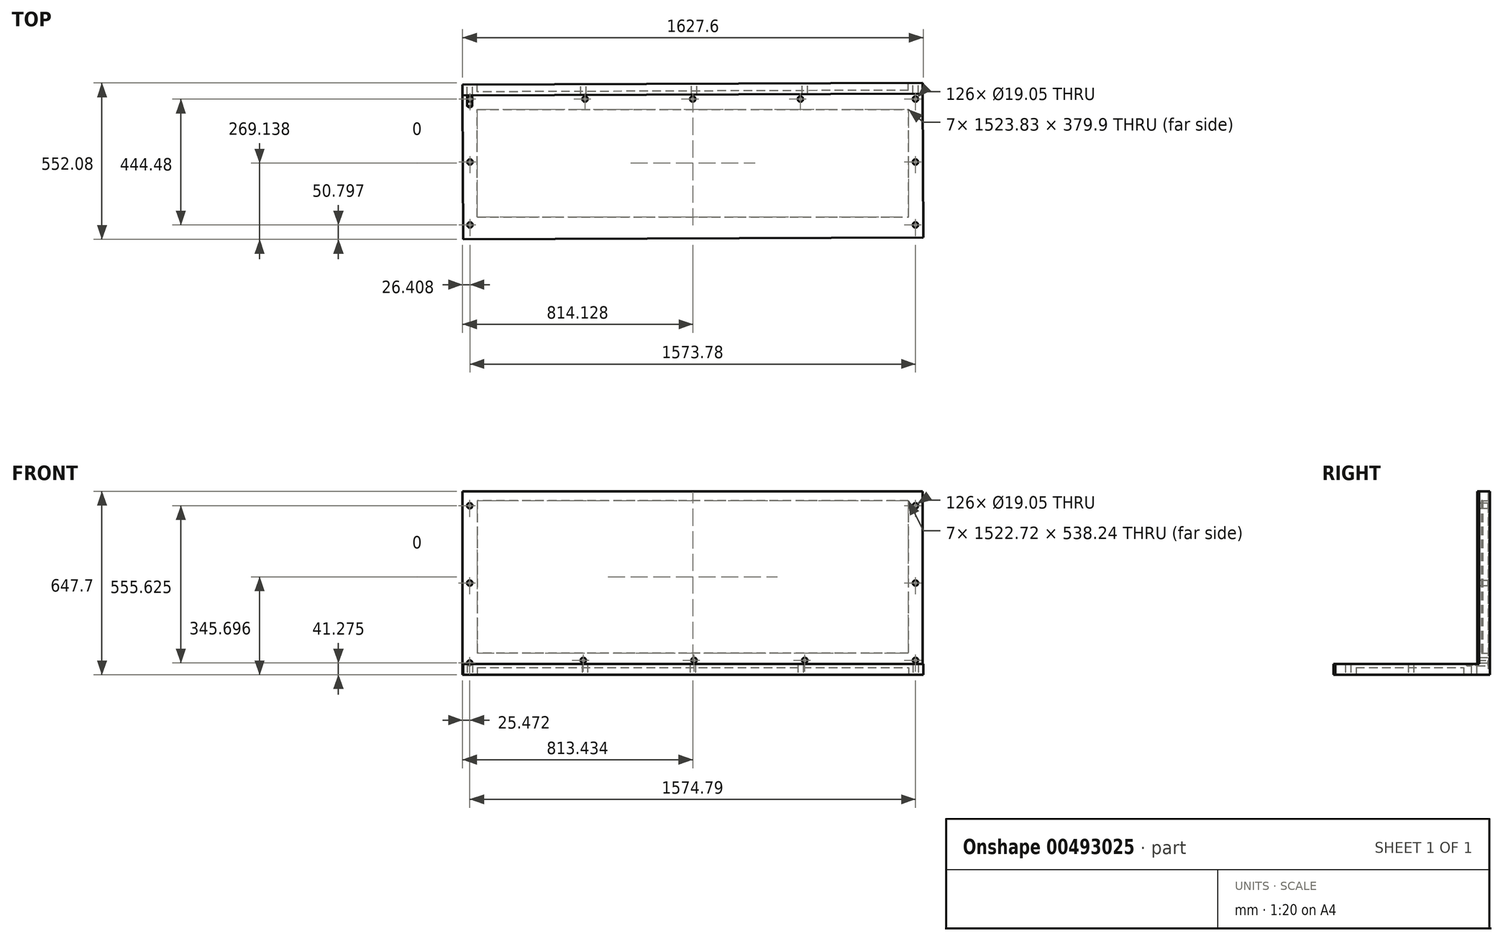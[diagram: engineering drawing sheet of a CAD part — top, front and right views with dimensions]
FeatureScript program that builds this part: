
annotation { "Feature Type Name" : "Feature", "Feature Type Description" : "" }
export const myFeature = defineFeature(function(context is Context, id is Id, definition is map)
    precondition{}
    {
        {
            var Q0;
            Q0=qCreatedBy(makeId("Top.planeOp"),FACE);
            var sketch = newSketch(context, id + "F0", { "sketchPlane" : qUnion([Q0])});
            skLineSegment(sketch, "E0", {"start": v(-1490.15, -82.87) * mm, "end": v(-1490.15, -540.07) * mm});
            skLineSegment(sketch, "E1", {"start": v(-1490.15, -540.07) * mm, "end": v(-1452.05, -540.07) * mm});
            skLineSegment(sketch, "E2", {"start": v(-1490.15, -82.87) * mm, "end": v(33.85, -82.87) * mm});
            skLineSegment(sketch, "E3", {"start": v(33.85, -82.87) * mm, "end": v(33.85, -540.07) * mm});
            skLineSegment(sketch, "E4", {"start": v(33.85, -540.07) * mm, "end": v(-4.25, -540.07) * mm});
            skLineSegment(sketch, "E5", {"start": v(-1445.7, -127.32) * mm, "end": v(-1452.05, -540.07) * mm});
            skLineSegment(sketch, "E6", {"start": v(-10.6, -127.32) * mm, "end": v(-4.25, -540.07) * mm});
            skLineSegment(sketch, "E7", {"start": v(-1445.7, -127.32) * mm, "end": v(-750.38, -127.32) * mm});
            skLineSegment(sketch, "E8", {"start": v(-10.6, -127.32) * mm, "end": v(-705.93, -127.32) * mm});
            skLineSegment(sketch, "E9", {"start": v(-705.93, -127.32) * mm, "end": v(-709.1, -540.07) * mm});
            skLineSegment(sketch, "E10", {"start": v(-750.38, -127.32) * mm, "end": v(-747.2, -540.07) * mm});
            skLineSegment(sketch, "E11", {"start": v(-709.1, -540.07) * mm, "end": v(-747.2, -540.07) * mm});
            skLineSegment(sketch, "E12", {"start": v(33.85, -540.07) * mm, "end": v(33.85, -590.87) * mm});
            skLineSegment(sketch, "E13", {"start": v(82.6, -32.07) * mm, "end": v(84.65, -590.87) * mm});
            skLineSegment(sketch, "E14", {"start": v(-1540.94, -35.7) * mm, "end": v(-1540.94, -594.5) * mm});
            skLineSegment(sketch, "E15", {"start": v(-1540.94, -35.7) * mm, "end": v(82.6, -32.07) * mm});
            skLineSegment(sketch, "E16", {"start": v(-1540.94, -594.5) * mm, "end": v(84.65, -590.87) * mm});
            skSolve(sketch);
        }
        {
            var Q0;
            Q0=makeQuery(id+"F0.imprint","IMPRINT",FACE,{"disambiguationData":[TD([[makeQuery(id+"F0.imprint","IMPRINT",EDGE,{"derivedFrom":sQuery(id+"F0.wireOp",EDGE,"E0")}),-1.0]])]});
            extrude(context, id + "F1", {"entities" : qUnion([Q0]), "depth" : -609.6 * mm});
        }
        {
            var Q0;
            Q0=makeQuery(id+"F1.opExtrude","CAP_FACE",FACE,{"disambiguationData":[OSD([sQuery(id+"F0.wireOp",EDGE,"E0"),sQuery(id+"F0.wireOp",EDGE,"E1"),sQuery(id+"F0.wireOp",EDGE,"E2"),sQuery(id+"F0.wireOp",EDGE,"E3"),sQuery(id+"F0.wireOp",EDGE,"E4"),sQuery(id+"F0.wireOp",EDGE,"E5"),sQuery(id+"F0.wireOp",EDGE,"E6"),sQuery(id+"F0.wireOp",EDGE,"E7"),sQuery(id+"F0.wireOp",EDGE,"E8"),sQuery(id+"F0.wireOp",EDGE,"E9"),sQuery(id+"F0.wireOp",EDGE,"E10"),sQuery(id+"F0.wireOp",EDGE,"E11"),sQuery(id+"F0.wireOp",EDGE,"E13"),sQuery(id+"F0.wireOp",EDGE,"E14"),sQuery(id+"F0.wireOp",EDGE,"E15"),sQuery(id+"F0.wireOp",EDGE,"E16")])],"isStart":true});
            var sketch = newSketch(context, id + "F2", { "sketchPlane" : qUnion([Q0])});
            skLineSegment(sketch, "E17.bottom", {"start": v(-653.62, -154.54) * mm, "end": v(-44.02, -154.54) * mm});
            skLineSegment(sketch, "E17.top", {"start": v(-653.62, -539.96) * mm, "end": v(-44.02, -539.96) * mm});
            skLineSegment(sketch, "E17.left", {"start": v(-653.62, -154.54) * mm, "end": v(-653.62, -539.96) * mm});
            skLineSegment(sketch, "E17.right", {"start": v(-44.02, -154.54) * mm, "end": v(-44.02, -539.96) * mm});
            skLineSegment(sketch, "E18.bottom", {"start": v(-791.66, -154.54) * mm, "end": v(-1401.26, -154.54) * mm});
            skLineSegment(sketch, "E18.top", {"start": v(-791.66, -534.45) * mm, "end": v(-1401.26, -534.45) * mm});
            skLineSegment(sketch, "E18.left", {"start": v(-791.66, -154.54) * mm, "end": v(-791.66, -534.45) * mm});
            skLineSegment(sketch, "E18.right", {"start": v(-1401.26, -154.54) * mm, "end": v(-1401.26, -534.45) * mm});
            skSolve(sketch);
        }
        {
            var Q0;
            Q0=makeQuery(id+"F2.imprint","IMPRINT",FACE,{"disambiguationData":[TD([[makeQuery(id+"F2.imprint","IMPRINT",EDGE,{"derivedFrom":sQuery(id+"F2.wireOp",EDGE,"E18.bottom")}),1.0]])]});
            extrude(context, id + "F3", {"entities" : qUnion([Q0]), "operationType" : NewBodyOperationType.REMOVE, "oppositeDirection" : true, "depth" : 609.6 * mm});
        }
        {
            var Q0;
            Q0=makeQuery(id+"F1.opExtrude","CAP_FACE",FACE,{"disambiguationData":[OSD([sQuery(id+"F0.wireOp",EDGE,"E0"),sQuery(id+"F0.wireOp",EDGE,"E1"),sQuery(id+"F0.wireOp",EDGE,"E2"),sQuery(id+"F0.wireOp",EDGE,"E3"),sQuery(id+"F0.wireOp",EDGE,"E4"),sQuery(id+"F0.wireOp",EDGE,"E5"),sQuery(id+"F0.wireOp",EDGE,"E6"),sQuery(id+"F0.wireOp",EDGE,"E7"),sQuery(id+"F0.wireOp",EDGE,"E8"),sQuery(id+"F0.wireOp",EDGE,"E9"),sQuery(id+"F0.wireOp",EDGE,"E10"),sQuery(id+"F0.wireOp",EDGE,"E11"),sQuery(id+"F0.wireOp",EDGE,"E13"),sQuery(id+"F0.wireOp",EDGE,"E14"),sQuery(id+"F0.wireOp",EDGE,"E15"),sQuery(id+"F0.wireOp",EDGE,"E16")])],"isStart":true});
            var sketch = newSketch(context, id + "F4", { "sketchPlane" : qUnion([Q0])});
            skLineSegment(sketch, "E19.bottom", {"start": v(-667.58, -154.54) * mm, "end": v(-57.98, -154.54) * mm});
            skLineSegment(sketch, "E19.top", {"start": v(-667.58, -534.45) * mm, "end": v(-57.98, -534.45) * mm});
            skLineSegment(sketch, "E19.left", {"start": v(-667.58, -154.54) * mm, "end": v(-667.58, -534.45) * mm});
            skLineSegment(sketch, "E19.right", {"start": v(-57.98, -154.54) * mm, "end": v(-57.98, -534.45) * mm});
            skSolve(sketch);
        }
        {
            var Q0;
            Q0=makeQuery(id+"F4.imprint","IMPRINT",FACE,{"disambiguationData":[TD([[makeQuery(id+"F4.imprint","IMPRINT",EDGE,{"derivedFrom":sQuery(id+"F4.wireOp",EDGE,"E19.bottom")}),-1.0]])]});
            extrude(context, id + "F5", {"entities" : qUnion([Q0]), "operationType" : NewBodyOperationType.REMOVE, "oppositeDirection" : true, "depth" : 609.6 * mm});
        }
        {
            var Q0;
            Q0=makeQuery(id+"F1.opExtrude","CAP_FACE",FACE,{"disambiguationData":[OSD([sQuery(id+"F0.wireOp",EDGE,"E0"),sQuery(id+"F0.wireOp",EDGE,"E1"),sQuery(id+"F0.wireOp",EDGE,"E2"),sQuery(id+"F0.wireOp",EDGE,"E3"),sQuery(id+"F0.wireOp",EDGE,"E4"),sQuery(id+"F0.wireOp",EDGE,"E5"),sQuery(id+"F0.wireOp",EDGE,"E6"),sQuery(id+"F0.wireOp",EDGE,"E7"),sQuery(id+"F0.wireOp",EDGE,"E8"),sQuery(id+"F0.wireOp",EDGE,"E9"),sQuery(id+"F0.wireOp",EDGE,"E10"),sQuery(id+"F0.wireOp",EDGE,"E11"),sQuery(id+"F0.wireOp",EDGE,"E13"),sQuery(id+"F0.wireOp",EDGE,"E14"),sQuery(id+"F0.wireOp",EDGE,"E15"),sQuery(id+"F0.wireOp",EDGE,"E16")])],"isStart":true});
            var sketch = newSketch(context, id + "F6", { "sketchPlane" : qUnion([Q0])});
            skLineSegment(sketch, "E20", {"start": v(-1540.94, -82.87) * mm, "end": v(82.78, -82.87) * mm});
            skLineSegment(sketch, "E21", {"start": v(82.78, -82.87) * mm, "end": v(82.6, -32.07) * mm});
            skLineSegment(sketch, "E22", {"start": v(-1540.94, -35.7) * mm, "end": v(82.6, -32.07) * mm});
            skLineSegment(sketch, "E23", {"start": v(-1540.94, -35.7) * mm, "end": v(-1540.94, -82.87) * mm});
            skSolve(sketch);
        }
        {
            var Q0;
            Q0=qSketchRegion(id+"F6",true);
            extrude(context, id + "F7", {"entities" : qUnion([Q0]), "operationType" : NewBodyOperationType.REMOVE, "oppositeDirection" : true, "depth" : 609.6 * mm});
        }
        {
            var Q0;
            Q0=makeQuery(id+"F1.opExtrude","SWEPT_FACE",FACE,{"disambiguationData":[OSD([sQuery(id+"F0.wireOp",EDGE,"E13")])]});
            var sketch = newSketch(context, id + "F8", { "sketchPlane" : qUnion([Q0])});
            skLineSegment(sketch, "E24.bottom", {"start": v(-38.1, 0) * mm, "end": v(0, 0) * mm});
            skLineSegment(sketch, "E24.top", {"start": v(-38.1, -609.6) * mm, "end": v(0, -609.6) * mm});
            skLineSegment(sketch, "E24.left", {"start": v(-38.1, 0) * mm, "end": v(-38.1, -609.6) * mm});
            skLineSegment(sketch, "E24.right", {"start": v(0, 0) * mm, "end": v(0, -609.6) * mm});
            skLineSegment(sketch, "E25.bottom", {"start": v(0, -609.6) * mm, "end": v(-546.1, -609.6) * mm});
            skLineSegment(sketch, "E25.top", {"start": v(0, -647.7) * mm, "end": v(-546.1, -647.7) * mm});
            skLineSegment(sketch, "E25.left", {"start": v(0, -609.6) * mm, "end": v(0, -647.7) * mm});
            skLineSegment(sketch, "E25.right", {"start": v(-546.1, -609.6) * mm, "end": v(-546.1, -647.7) * mm});
            skSolve(sketch);
        }
        {
            var Q0;
            Q0=makeQuery(id+"F8.imprint","IMPRINT",FACE,{"disambiguationData":[TD([[makeQuery(id+"F8.imprint","IMPRINT",EDGE,{"derivedFrom":sQuery(id+"F8.wireOp",EDGE,"E24.bottom")}),-1.0]])]});
            var Q1;
            Q1=makeQuery(id+"F8.imprint","IMPRINT",FACE,{"disambiguationData":[TD([[makeQuery(id+"F8.imprint","IMPRINT",EDGE,{"derivedFrom":sQuery(id+"F8.wireOp",EDGE,"E25.top")}),-1.0]])]});
            extrude(context, id + "F9", {"entities" : qUnion([Q0, Q1]), "operationType" : NewBodyOperationType.ADD, "depth" : 1625.6 * mm});
        }
        {
            var Q0;
            Q0=makeQuery(id+"F9.opExtrude","SWEPT_BODY",BODY,{"disambiguationData":[OSD([sQuery(id+"F8.wireOp",EDGE,"E24.bottom"),sQuery(id+"F8.wireOp",EDGE,"E24.left"),sQuery(id+"F8.wireOp",EDGE,"E24.right"),sQuery(id+"F8.wireOp",EDGE,"E25.bottom"),sQuery(id+"F8.wireOp",EDGE,"E25.top"),sQuery(id+"F8.wireOp",EDGE,"E25.left"),sQuery(id+"F8.wireOp",EDGE,"E25.right")])]});
            transform(context, id + "F10", {"entities" : qUnion([Q0]), "transformType" : TransformType.TRANSLATION_3D, "dx" : -1625.6 * mm, "dy" : 254 * mm, "dz" : -254 * mm, "makeCopy" : false});
        }
        {
            var Q0;
            Q0=makeQuery(id+"F1.opExtrude","SWEPT_FACE",FACE,{"disambiguationData":[OSD([sQuery(id+"F0.wireOp",EDGE,"E16")])]});
            var sketch = newSketch(context, id + "F11", { "sketchPlane" : qUnion([Q0])});
            skLineSegment(sketch, "E26", {"start": v(-1465.88, 0) * mm, "end": v(-1465.88, -25.4) * mm});
            skLineSegment(sketch, "E27", {"start": v(-1465.88, -609.6) * mm, "end": v(-1465.88, -584.2) * mm});
            skLineSegment(sketch, "E28", {"start": v(83.33, -561.8) * mm, "end": v(57.93, -561.8) * mm});
            skLineSegment(sketch, "E29", {"start": v(-1542.27, -290.2) * mm, "end": v(-1516.87, -290.2) * mm});
            skLineSegment(sketch, "E30.bottom", {"start": v(-1516.87, -25.4) * mm, "end": v(57.75, -25.4) * mm});
            skLineSegment(sketch, "E30.top", {"start": v(-1516.87, -583.33) * mm, "end": v(57.75, -583.33) * mm});
            skLineSegment(sketch, "E30.left", {"start": v(-1516.87, -25.4) * mm, "end": v(-1516.87, -583.33) * mm});
            skLineSegment(sketch, "E30.right", {"start": v(57.75, -25.4) * mm, "end": v(57.75, -583.33) * mm});
            skSolve(sketch);
        }
        {
            var Q0;
            Q0=qSketchRegion(id+"F11",true);
            extrude(context, id + "F12", {"entities" : qUnion([Q0]), "operationType" : NewBodyOperationType.REMOVE, "oppositeDirection" : true, "depth" : 25.4 * mm});
        }
        {
            var Q0;
            Q0=makeQuery(id+"F1.opExtrude","SWEPT_FACE",FACE,{"disambiguationData":[OSD([sQuery(id+"F0.wireOp",EDGE,"E13")])]});
            var sketch = newSketch(context, id + "F13", { "sketchPlane" : qUnion([Q0])});
            skLineSegment(sketch, "E31", {"start": v(-591.17, -58.34) * mm, "end": v(-565.77, -58.34) * mm});
            skLineSegment(sketch, "E32", {"start": v(-337.17, 0) * mm, "end": v(-337.17, -25.4) * mm});
            skLineSegment(sketch, "E33", {"start": v(-83.17, -304.8) * mm, "end": v(-108.57, -304.8) * mm});
            skLineSegment(sketch, "E34", {"start": v(-337.17, -609.6) * mm, "end": v(-337.17, -584.2) * mm});
            skLineSegment(sketch, "E35.bottom", {"start": v(-565.77, -25.4) * mm, "end": v(-109.45, -25.4) * mm});
            skLineSegment(sketch, "E35.top", {"start": v(-565.77, -581.67) * mm, "end": v(-109.45, -581.67) * mm});
            skLineSegment(sketch, "E35.left", {"start": v(-565.77, -25.4) * mm, "end": v(-565.77, -581.67) * mm});
            skLineSegment(sketch, "E35.right", {"start": v(-109.45, -25.4) * mm, "end": v(-109.45, -581.67) * mm});
            skSolve(sketch);
        }
        {
            var Q0;
            Q0=qSketchRegion(id+"F13",true);
            extrude(context, id + "F14", {"entities" : qUnion([Q0]), "operationType" : NewBodyOperationType.REMOVE, "oppositeDirection" : true, "depth" : 25.4 * mm});
        }
        {
            var Q0;
            Q0=makeQuery(id+"F1.opExtrude","SWEPT_FACE",FACE,{"disambiguationData":[OSD([sQuery(id+"F0.wireOp",EDGE,"E14")])]});
            var sketch = newSketch(context, id + "F15", { "sketchPlane" : qUnion([Q0])});
            skLineSegment(sketch, "E36", {"start": v(82.87, -290.2) * mm, "end": v(108.27, -290.2) * mm});
            skLineSegment(sketch, "E37", {"start": v(338.69, 0) * mm, "end": v(338.69, -25.22) * mm});
            skLineSegment(sketch, "E38", {"start": v(594.5, -276.95) * mm, "end": v(569.1, -276.95) * mm});
            skLineSegment(sketch, "E39", {"start": v(338.69, -609.6) * mm, "end": v(338.69, -584.2) * mm});
            skLineSegment(sketch, "E40.bottom", {"start": v(108.27, -25.22) * mm, "end": v(567.89, -25.22) * mm});
            skLineSegment(sketch, "E40.top", {"start": v(108.27, -581.67) * mm, "end": v(567.89, -581.67) * mm});
            skLineSegment(sketch, "E40.left", {"start": v(108.27, -25.22) * mm, "end": v(108.27, -581.67) * mm});
            skLineSegment(sketch, "E40.right", {"start": v(567.89, -25.22) * mm, "end": v(567.89, -581.67) * mm});
            skSolve(sketch);
        }
        {
            var Q0;
            Q0=qSketchRegion(id+"F15",true);
            extrude(context, id + "F16", {"entities" : qUnion([Q0]), "operationType" : NewBodyOperationType.REMOVE, "oppositeDirection" : true, "depth" : 25.4 * mm});
        }
        {
            var Q0;
            Q0=makeQuery(id+"F9.opExtrude","SWEPT_FACE",FACE,{"disambiguationData":[OSD([sQuery(id+"F8.wireOp",EDGE,"E24.right"),sQuery(id+"F8.wireOp",EDGE,"E25.left")])]});
            var sketch = newSketch(context, id + "F17", { "sketchPlane" : qUnion([Q0])});
            skPoint(sketch, "E41", {"position": v(-58.02, -304.8) * mm});
            skPoint(sketch, "E42", {"position": v(-58.02, -577.85) * mm});
            skPoint(sketch, "E43", {"position": v(-58.02, -850.9) * mm});
            skSolve(sketch);
        }
        {
            var Q0;
            Q0=sQuery(id+"F17.wireOp",VERTEX,"E41");
            var Q1;
            Q1=sQuery(id+"F17.wireOp",VERTEX,"E42");
            var Q2;
            Q2=sQuery(id+"F17.wireOp",VERTEX,"E43");
            var Q3;
            Q3=makeQuery(id+"F9.opExtrude","SWEPT_BODY",BODY,{"disambiguationData":[OSD([sQuery(id+"F8.wireOp",EDGE,"E24.bottom"),sQuery(id+"F8.wireOp",EDGE,"E24.left"),sQuery(id+"F8.wireOp",EDGE,"E24.right"),sQuery(id+"F8.wireOp",EDGE,"E25.bottom"),sQuery(id+"F8.wireOp",EDGE,"E25.top"),sQuery(id+"F8.wireOp",EDGE,"E25.left"),sQuery(id+"F8.wireOp",EDGE,"E25.right")])]});
            hole(context, id + "F18", {"style" : HoleStyle.SIMPLE, "endStyle" : HoleEndStyle.BLIND, "holeDiameter" : 19.05 * mm, "holeDepth" : 76.2 * mm, "isTappedThrough" : true, "tappedDepth" : 12.7 * mm, "tapClearance" : 3, "locations" : qUnion([Q0, Q1, Q2]), "scope" : qUnion([Q3])});
        }
        {
            var Q0;
            Q0=makeQuery(id+"F9.opExtrude","SWEPT_FACE",FACE,{"disambiguationData":[OSD([sQuery(id+"F8.wireOp",EDGE,"E24.right"),sQuery(id+"F8.wireOp",EDGE,"E25.left")])]});
            var sketch = newSketch(context, id + "F19", { "sketchPlane" : qUnion([Q0])});
            skPoint(sketch, "E44", {"position": v(333.14, -850.9) * mm});
            skPoint(sketch, "E45", {"position": v(724.3, -850.9) * mm});
            skPoint(sketch, "E46", {"position": v(1115.46, -850.9) * mm});
            skPoint(sketch, "E47", {"position": v(1516.78, -860.42) * mm});
            skPoint(sketch, "E48", {"position": v(1516.78, -577.85) * mm});
            skPoint(sketch, "E49", {"position": v(1516.78, -304.8) * mm});
            skSolve(sketch);
        }
        {
            var Q0;
            Q0=sQuery(id+"F19.wireOp",VERTEX,"E44");
            var Q1;
            Q1=sQuery(id+"F19.wireOp",VERTEX,"E45");
            var Q2;
            Q2=sQuery(id+"F19.wireOp",VERTEX,"E46");
            var Q3;
            Q3=sQuery(id+"F19.wireOp",VERTEX,"E47");
            var Q4;
            Q4=sQuery(id+"F19.wireOp",VERTEX,"E48");
            var Q5;
            Q5=sQuery(id+"F19.wireOp",VERTEX,"E49");
            var Q6;
            Q6=makeQuery(id+"F9.opExtrude","SWEPT_BODY",BODY,{"disambiguationData":[OSD([sQuery(id+"F8.wireOp",EDGE,"E24.bottom"),sQuery(id+"F8.wireOp",EDGE,"E24.left"),sQuery(id+"F8.wireOp",EDGE,"E24.right"),sQuery(id+"F8.wireOp",EDGE,"E25.bottom"),sQuery(id+"F8.wireOp",EDGE,"E25.top"),sQuery(id+"F8.wireOp",EDGE,"E25.left"),sQuery(id+"F8.wireOp",EDGE,"E25.right")])]});
            hole(context, id + "F20", {"style" : HoleStyle.SIMPLE, "endStyle" : HoleEndStyle.BLIND, "holeDiameter" : 19.05 * mm, "holeDepth" : 76.2 * mm, "isTappedThrough" : true, "tappedDepth" : 12.7 * mm, "tapClearance" : 3, "locations" : qUnion([Q0, Q1, Q2, Q3, Q4, Q5]), "scope" : qUnion([Q6])});
        }
        {
            var Q0;
            Q0=makeQuery(id+"F9.opExtrude","SWEPT_FACE",FACE,{"disambiguationData":[OSD([sQuery(id+"F8.wireOp",EDGE,"E24.right"),sQuery(id+"F8.wireOp",EDGE,"E25.left")])]});
            var sketch = newSketch(context, id + "F21", { "sketchPlane" : qUnion([Q0])});
            skLineSegment(sketch, "E50", {"start": v(-83.42, -374.66) * mm, "end": v(-32.62, -374.66) * mm});
            skLineSegment(sketch, "E51", {"start": v(0, -901.7) * mm, "end": v(0, -825.5) * mm});
            skLineSegment(sketch, "E52", {"start": v(1542.18, -649.58) * mm, "end": v(1491.38, -649.58) * mm});
            skLineSegment(sketch, "E53.bottom", {"start": v(-32.62, -286.88) * mm, "end": v(1490.1, -286.88) * mm});
            skLineSegment(sketch, "E53.top", {"start": v(-32.62, -825.12) * mm, "end": v(1490.1, -825.12) * mm});
            skLineSegment(sketch, "E53.left", {"start": v(-32.62, -286.88) * mm, "end": v(-32.62, -825.12) * mm});
            skLineSegment(sketch, "E53.right", {"start": v(1490.1, -286.88) * mm, "end": v(1490.1, -825.12) * mm});
            skSolve(sketch);
        }
        {
            var Q0;
            {var subQ3=sQuery(id+"F21.wireOp",EDGE,"E53.bottom");Q0=makeQuery(id+"F21.imprint","IMPRINT",FACE,{"disambiguationData":[TD([[makeQuery(id+"F21.imprint","IMPRINT",EDGE,{"derivedFrom":subQ3}),-1.0]])]});}
            extrude(context, id + "F22", {"entities" : qUnion([Q0]), "operationType" : NewBodyOperationType.REMOVE, "oppositeDirection" : true, "depth" : 25.4 * mm});
        }
        {
            var Q0;
            Q0=makeQuery(id+"F9.opExtrude","SWEPT_FACE",FACE,{"disambiguationData":[OSD([sQuery(id+"F8.wireOp",EDGE,"E25.top")])]});
            var sketch = newSketch(context, id + "F23", { "sketchPlane" : qUnion([Q0])});
            skLineSegment(sketch, "E54", {"start": v(-1491.32, 18.75) * mm, "end": v(-1516.72, 18.75) * mm});
            skLineSegment(sketch, "E55", {"start": v(-1491.32, 241) * mm, "end": v(-1516.72, 241) * mm});
            skLineSegment(sketch, "E56", {"start": v(-1491.32, -203.49) * mm, "end": v(-1516.72, -203.49) * mm});
            skLineSegment(sketch, "E57", {"start": v(31.66, 241) * mm, "end": v(57.06, 241) * mm});
            skLineSegment(sketch, "E58", {"start": v(31.66, 18.75) * mm, "end": v(57.06, 18.75) * mm});
            skLineSegment(sketch, "E59", {"start": v(31.66, -203.49) * mm, "end": v(57.06, -203.49) * mm});
            skPoint(sketch, "E60", {"position": v(-1516.72, 241) * mm});
            skPoint(sketch, "E61", {"position": v(-1516.72, 18.75) * mm});
            skPoint(sketch, "E62", {"position": v(-1516.72, -203.49) * mm});
            skLineSegment(sketch, "E63", {"start": v(-1491.32, -203.49) * mm, "end": v(-1491.32, -228.89) * mm});
            skLineSegment(sketch, "E64", {"start": v(-1491.32, -228.89) * mm, "end": v(-1110.32, -228.89) * mm});
            skLineSegment(sketch, "E65", {"start": v(31.66, -203.49) * mm, "end": v(31.66, -228.89) * mm});
            skLineSegment(sketch, "E66", {"start": v(31.66, -228.89) * mm, "end": v(-349.34, -228.89) * mm});
            skLineSegment(sketch, "E67", {"start": v(-1110.32, -228.89) * mm, "end": v(-729.83, -228.89) * mm});
            skPoint(sketch, "E68", {"position": v(-1110.32, -228.89) * mm});
            skPoint(sketch, "E69", {"position": v(-729.83, -228.89) * mm});
            skPoint(sketch, "E70", {"position": v(-349.34, -228.89) * mm});
            skPoint(sketch, "E71", {"position": v(31.66, -228.89) * mm});
            skPoint(sketch, "E72", {"position": v(-1491.32, -228.89) * mm});
            skPoint(sketch, "E73", {"position": v(57.06, -203.49) * mm});
            skPoint(sketch, "E74", {"position": v(57.06, 18.75) * mm});
            skPoint(sketch, "E75", {"position": v(57.06, 241) * mm});
            skPoint(sketch, "E76", {"position": v(-1110.32, -203.49) * mm});
            skPoint(sketch, "E77", {"position": v(-729.83, -203.49) * mm});
            skPoint(sketch, "E78", {"position": v(-349.34, -203.49) * mm});
            skSolve(sketch);
        }
        {
            var Q0;
            Q0=sQuery(id+"F23.wireOp",VERTEX,"E60");
            var Q1;
            Q1=sQuery(id+"F23.wireOp",VERTEX,"E61");
            var Q2;
            Q2=sQuery(id+"F23.wireOp",VERTEX,"E62");
            var Q3;
            Q3=sQuery(id+"F23.wireOp",VERTEX,"E76");
            var Q4;
            Q4=sQuery(id+"F23.wireOp",VERTEX,"E78");
            var Q5;
            Q5=sQuery(id+"F23.wireOp",VERTEX,"E77");
            var Q6;
            Q6=sQuery(id+"F23.wireOp",VERTEX,"E73");
            var Q7;
            Q7=sQuery(id+"F23.wireOp",VERTEX,"E74");
            var Q8;
            Q8=sQuery(id+"F23.wireOp",VERTEX,"E75");
            var Q9;
            Q9=makeQuery(id+"F9.opExtrude","SWEPT_BODY",BODY,{"disambiguationData":[OSD([sQuery(id+"F8.wireOp",EDGE,"E24.bottom"),sQuery(id+"F8.wireOp",EDGE,"E24.left"),sQuery(id+"F8.wireOp",EDGE,"E24.right"),sQuery(id+"F8.wireOp",EDGE,"E25.bottom"),sQuery(id+"F8.wireOp",EDGE,"E25.top"),sQuery(id+"F8.wireOp",EDGE,"E25.left"),sQuery(id+"F8.wireOp",EDGE,"E25.right")])]});
            hole(context, id + "F24", {"style" : HoleStyle.SIMPLE, "endStyle" : HoleEndStyle.BLIND, "holeDiameter" : 19.05 * mm, "holeDepth" : 76.2 * mm, "isTappedThrough" : true, "tappedDepth" : 12.7 * mm, "tapClearance" : 3, "locations" : qUnion([Q0, Q1, Q2, Q3, Q4, Q5, Q6, Q7, Q8]), "scope" : qUnion([Q9])});
        }
        {
            var Q0;
            Q0=makeQuery(id+"F9.opExtrude","SWEPT_FACE",FACE,{"disambiguationData":[OSD([sQuery(id+"F8.wireOp",EDGE,"E25.top")])]});
            var sketch = newSketch(context, id + "F25", { "sketchPlane" : qUnion([Q0])});
            skLineSegment(sketch, "E79", {"start": v(-1541.71, 129.47) * mm, "end": v(-1490.91, 129.28) * mm});
            skLineSegment(sketch, "E80", {"start": v(83.71, 78.8) * mm, "end": v(32.91, 78.98) * mm});
            skLineSegment(sketch, "E81", {"start": v(-728.32, 288.8) * mm, "end": v(-728.32, 212.6) * mm});
            skLineSegment(sketch, "E82.bottom", {"start": v(-1490.91, 212.6) * mm, "end": v(32.91, 212.6) * mm});
            skLineSegment(sketch, "E82.top", {"start": v(-1490.91, -167.3) * mm, "end": v(32.91, -167.3) * mm});
            skLineSegment(sketch, "E82.left", {"start": v(-1490.91, 212.6) * mm, "end": v(-1490.91, -167.3) * mm});
            skLineSegment(sketch, "E82.right", {"start": v(32.91, 212.6) * mm, "end": v(32.91, -167.3) * mm});
            skSolve(sketch);
        }
        {
            var Q0;
            {var subQ4=sQuery(id+"F25.wireOp",EDGE,"E82.top");Q0=makeQuery(id+"F25.imprint","IMPRINT",FACE,{"disambiguationData":[TD([[makeQuery(id+"F25.imprint","IMPRINT",EDGE,{"derivedFrom":subQ4}),1.0]])]});}
            extrude(context, id + "F26", {"entities" : qUnion([Q0]), "operationType" : NewBodyOperationType.REMOVE, "oppositeDirection" : true, "depth" : 25.4 * mm});
        }
        {
            var Q0;
            Q0=makeQuery(id+"F1.opExtrude","SWEPT_BODY",BODY,{"disambiguationData":[OSD([sQuery(id+"F0.wireOp",EDGE,"E0"),sQuery(id+"F0.wireOp",EDGE,"E1"),sQuery(id+"F0.wireOp",EDGE,"E2"),sQuery(id+"F0.wireOp",EDGE,"E3"),sQuery(id+"F0.wireOp",EDGE,"E4"),sQuery(id+"F0.wireOp",EDGE,"E5"),sQuery(id+"F0.wireOp",EDGE,"E6"),sQuery(id+"F0.wireOp",EDGE,"E7"),sQuery(id+"F0.wireOp",EDGE,"E8"),sQuery(id+"F0.wireOp",EDGE,"E9"),sQuery(id+"F0.wireOp",EDGE,"E10"),sQuery(id+"F0.wireOp",EDGE,"E11"),sQuery(id+"F0.wireOp",EDGE,"E13"),sQuery(id+"F0.wireOp",EDGE,"E14"),sQuery(id+"F0.wireOp",EDGE,"E15"),sQuery(id+"F0.wireOp",EDGE,"E16")])]});
            deleteBodies(context, id + "F27", {"entities" : qUnion([Q0])});
        }
    });
